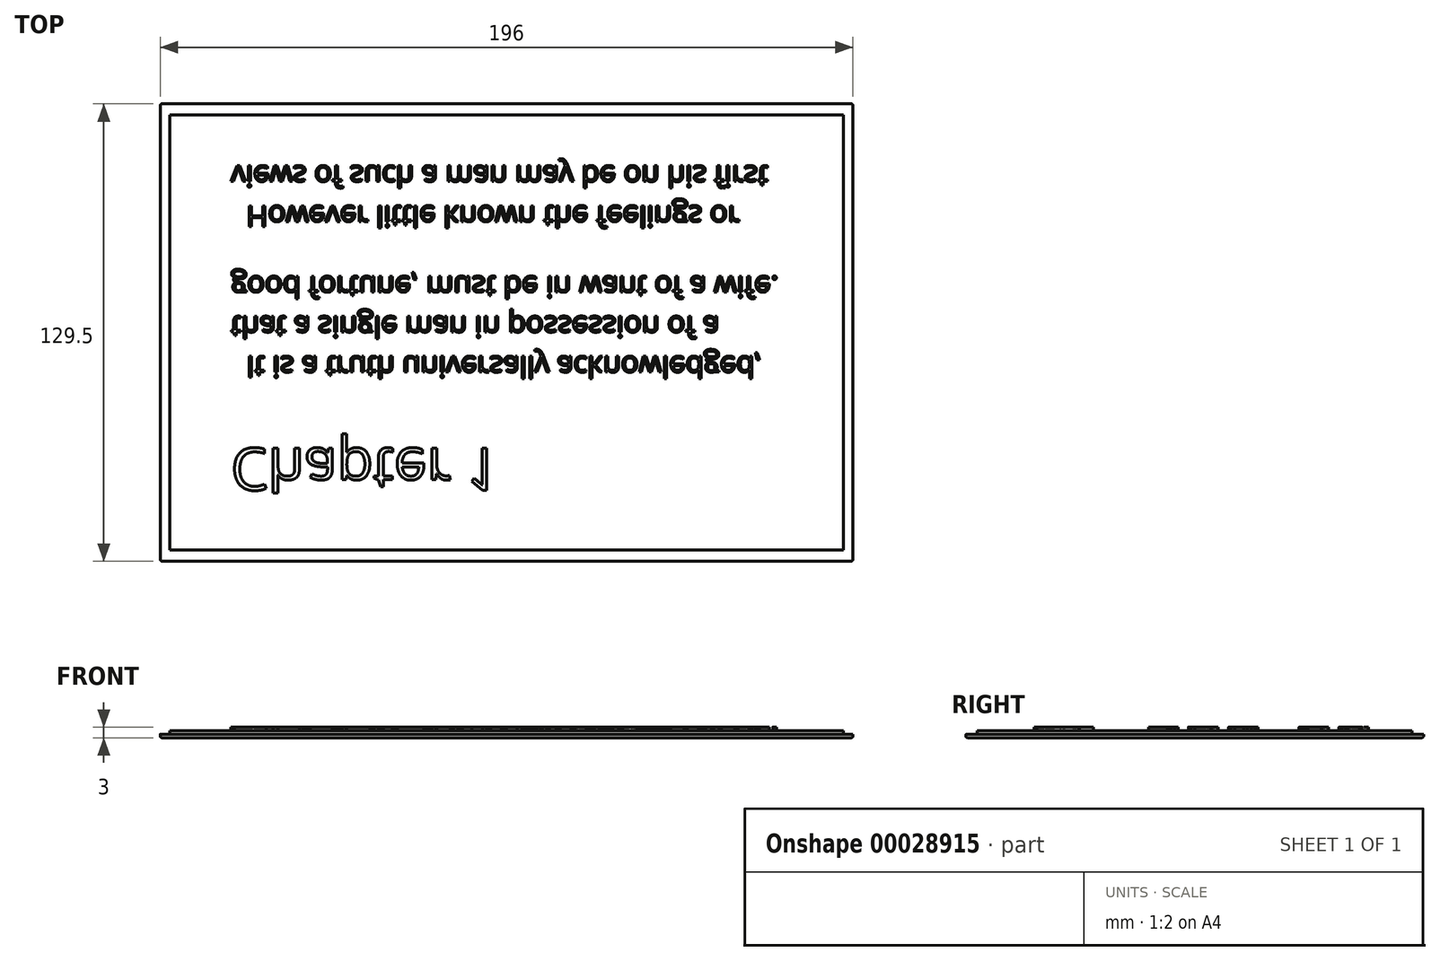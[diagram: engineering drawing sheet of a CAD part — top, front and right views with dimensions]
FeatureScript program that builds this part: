
annotation { "Feature Type Name" : "Feature", "Feature Type Description" : "" }
export const myFeature = defineFeature(function(context is Context, id is Id, definition is map)
    precondition{}
    {
        {
            assignVariable(context, id + "F0", {"name" : "TypeH", "anyValue" : 3});
        }
        {
            var Q0;
            Q0=qCreatedBy(makeId("Top.planeOp"),FACE);
            var sketch = newSketch(context, id + "F1", { "sketchPlane" : qUnion([Q0])});
            skLineSegment(sketch, "E0.bottom", {"start": v(0, 129.5) * mm, "end": v(196, 129.5) * mm});
            skLineSegment(sketch, "E0.top", {"start": v(0, 0) * mm, "end": v(196, 0) * mm});
            skLineSegment(sketch, "E0.left", {"start": v(0, 129.5) * mm, "end": v(0, 0) * mm});
            skLineSegment(sketch, "E0.right", {"start": v(196, 129.5) * mm, "end": v(196, 0) * mm});
            skSolve(sketch);
        }
        {
            var Q0;
            Q0=makeQuery(id+"F1.imprint","IMPRINT",FACE,{"disambiguationData":[TD([[makeQuery(id+"F1.imprint","IMPRINT",EDGE,{"derivedFrom":sQuery(id+"F1.wireOp",EDGE,"E0.bottom")}),-1.0]])]});
            extrude(context, id + "F2", {"entities" : qUnion([Q0]), "oppositeDirection" : true, "depth" : (getVariable(context, 'TypeH') - 1) * mm});
        }
        {
            var Q0;
            Q0=makeQuery(id+"F2.opExtrude","CAP_FACE",FACE,{"disambiguationData":[OSD([sQuery(id+"F1.wireOp",EDGE,"E0.bottom"),sQuery(id+"F1.wireOp",EDGE,"E0.top"),sQuery(id+"F1.wireOp",EDGE,"E0.left"),sQuery(id+"F1.wireOp",EDGE,"E0.right")])],"isStart":false});
            var sketch = newSketch(context, id + "F3", { "sketchPlane" : qUnion([Q0])});
            skLineSegment(sketch, "E1.bottom", {"start": v(2.7, -126.3) * mm, "end": v(193.3, -126.3) * mm});
            skLineSegment(sketch, "E1.top", {"start": v(2.7, -3.2) * mm, "end": v(193.3, -3.2) * mm});
            skLineSegment(sketch, "E1.left", {"start": v(2.7, -126.3) * mm, "end": v(2.7, -3.2) * mm});
            skLineSegment(sketch, "E1.right", {"start": v(193.3, -126.3) * mm, "end": v(193.3, -3.2) * mm});
            skSolve(sketch);
        }
        {
            var Q0;
            Q0=makeQuery(id+"F3.imprint","IMPRINT",FACE,{"disambiguationData":[TD([[makeQuery(id+"F3.imprint","IMPRINT",EDGE,{"derivedFrom":sQuery(id+"F3.wireOp",EDGE,"E1.bottom")}),-1.0]])]});
            extrude(context, id + "F4", {"entities" : qUnion([Q0]), "operationType" : NewBodyOperationType.REMOVE, "oppositeDirection" : true, "depth" : 1 * mm});
        }
        {
            var Q0;
            Q0=makeQuery(id+"F2.opExtrude","CAP_FACE",FACE,{"disambiguationData":[OSD([sQuery(id+"F1.wireOp",EDGE,"E0.bottom"),sQuery(id+"F1.wireOp",EDGE,"E0.top"),sQuery(id+"F1.wireOp",EDGE,"E0.left"),sQuery(id+"F1.wireOp",EDGE,"E0.right")])],"isStart":false});
            var sketch = newSketch(context, id + "F5", { "sketchPlane" : qUnion([Q0])});
            skText(sketch, "E2", { "text": "Chapter 1", "fontName": "OpenSans-Regular.ttf"});
            skLineSegment(sketch, "E3", {"start": v(20, -32) * mm, "end": v(20, -109.5) * mm, "construction": true});
            skText(sketch, "E4", { "text": "  It is a truth universally acknowledged,\nthat a single man in possession of a\ngood fortune, must be in want of a wife.", "fontName": "OpenSans-Regular.ttf"});
            skText(sketch, "E5", { "text": "  However little known the feelings or\nviews of such a man may be on his first", "fontName": "OpenSans-Regular.ttf"});
            const initialGuessF5  = {"E2": [0.02, -0.032, 1, 0, 0.012], "E4": [0.02, -0.058, 1, 0, 0.006], "E5": [0.02, -0.10063, 1, 0, 0.006]};
            skSetInitialGuess(sketch, initialGuessF5);
            skSolve(sketch);
        }
        {
            var Q0;
            Q0 = qSketchRegion(id + "F5", true);
            extrude(context, id + "F6", {"entities" : qUnion([Q0]), "operationType" : NewBodyOperationType.ADD, "depth" : 1 * mm});
        }
        {
            var Q0;
            Q0=makeQuery(id+"F2.opExtrude","SWEPT_BODY",BODY,{"disambiguationData":[OSD([sQuery(id+"F1.wireOp",EDGE,"E0.bottom"),sQuery(id+"F1.wireOp",EDGE,"E0.top"),sQuery(id+"F1.wireOp",EDGE,"E0.left"),sQuery(id+"F1.wireOp",EDGE,"E0.right")])]});
            var Q1;
            Q1=qCreatedBy(makeId("Top.planeOp"),FACE);
            mirror(context, id + "F7", {"entities" : qUnion([Q0]), "mirrorPlane" : qUnion([Q1])});
        }
        {
            var Q0;
            Q0=makeQuery(id+"F2.opExtrude","SWEPT_BODY",BODY,{"disambiguationData":[OSD([sQuery(id+"F1.wireOp",EDGE,"E0.bottom"),sQuery(id+"F1.wireOp",EDGE,"E0.top"),sQuery(id+"F1.wireOp",EDGE,"E0.left"),sQuery(id+"F1.wireOp",EDGE,"E0.right")])]});
            deleteBodies(context, id + "F8", {"entities" : qUnion([Q0])});
        }
        {
            var Q0;
            Q0=makeQuery(id+"F7.opPattern","COPY",EDGE,{"derivedFrom":makeQuery(id+"F2.opExtrude","SWEPT_EDGE",EDGE,{"disambiguationData":[OSD([sQuery(id+"F1.wireOp",EDGE,"E0.top"),sQuery(id+"F1.wireOp",EDGE,"E0.right")])]}),"instanceName":"1"});
            var Q1;
            Q1=makeQuery(id+"F7.opPattern","COPY",EDGE,{"derivedFrom":makeQuery(id+"F2.opExtrude","CAP_EDGE",EDGE,{"disambiguationData":[OSD([sQuery(id+"F1.wireOp",EDGE,"E0.top")])],"isStart":true}),"instanceName":"1"});
            var Q2;
            Q2=makeQuery(id+"F7.opPattern","COPY",EDGE,{"derivedFrom":makeQuery(id+"F2.opExtrude","CAP_EDGE",EDGE,{"disambiguationData":[OSD([sQuery(id+"F1.wireOp",EDGE,"E0.right")])],"isStart":true}),"instanceName":"1"});
            var Q3;
            Q3=makeQuery(id+"F7.opPattern","COPY",EDGE,{"derivedFrom":makeQuery(id+"F2.opExtrude","CAP_EDGE",EDGE,{"disambiguationData":[OSD([sQuery(id+"F1.wireOp",EDGE,"E0.bottom")])],"isStart":true}),"instanceName":"1"});
            var Q4;
            Q4=makeQuery(id+"F7.opPattern","COPY",EDGE,{"derivedFrom":makeQuery(id+"F2.opExtrude","CAP_EDGE",EDGE,{"disambiguationData":[OSD([sQuery(id+"F1.wireOp",EDGE,"E0.left")])],"isStart":true}),"instanceName":"1"});
            var Q5;
            Q5=makeQuery(id+"F7.opPattern","COPY",EDGE,{"derivedFrom":makeQuery(id+"F2.opExtrude","SWEPT_EDGE",EDGE,{"disambiguationData":[OSD([sQuery(id+"F1.wireOp",EDGE,"E0.top"),sQuery(id+"F1.wireOp",EDGE,"E0.left")])]}),"instanceName":"1"});
            var Q6;
            Q6=makeQuery(id+"F7.opPattern","COPY",EDGE,{"derivedFrom":makeQuery(id+"F2.opExtrude","SWEPT_EDGE",EDGE,{"disambiguationData":[OSD([sQuery(id+"F1.wireOp",EDGE,"E0.bottom"),sQuery(id+"F1.wireOp",EDGE,"E0.right")])]}),"instanceName":"1"});
            var Q7;
            Q7=makeQuery(id+"F7.opPattern","COPY",EDGE,{"derivedFrom":makeQuery(id+"F2.opExtrude","SWEPT_EDGE",EDGE,{"disambiguationData":[OSD([sQuery(id+"F1.wireOp",EDGE,"E0.bottom"),sQuery(id+"F1.wireOp",EDGE,"E0.left")])]}),"instanceName":"1"});
            var Q8;
            Q8=makeQuery(id+"F4.boolean.opBoolean","COPY",EDGE,{"derivedFrom":makeQuery(id+"F4.opExtrude","SWEPT_EDGE",EDGE,{"disambiguationData":[OSD([sQuery(id+"F3.wireOp",EDGE,"E1.bottom"),sQuery(id+"F3.wireOp",EDGE,"E1.left")])]})});
            var Q9;
            Q9=makeQuery(id+"F4.boolean.opBoolean","COPY",EDGE,{"derivedFrom":makeQuery(id+"F4.opExtrude","SWEPT_EDGE",EDGE,{"disambiguationData":[OSD([sQuery(id+"F3.wireOp",EDGE,"E1.bottom"),sQuery(id+"F3.wireOp",EDGE,"E1.right")])]})});
            var Q10;
            Q10=makeQuery(id+"F4.boolean.opBoolean","COPY",EDGE,{"derivedFrom":makeQuery(id+"F4.opExtrude","SWEPT_EDGE",EDGE,{"disambiguationData":[OSD([sQuery(id+"F3.wireOp",EDGE,"E1.top"),sQuery(id+"F3.wireOp",EDGE,"E1.right")])]})});
            var Q11;
            Q11=makeQuery(id+"F4.boolean.opBoolean","COPY",EDGE,{"derivedFrom":makeQuery(id+"F4.opExtrude","SWEPT_EDGE",EDGE,{"disambiguationData":[OSD([sQuery(id+"F3.wireOp",EDGE,"E1.top"),sQuery(id+"F3.wireOp",EDGE,"E1.left")])]})});
            fillet(context, id + "F9", {"entities" : qUnion([Q0, Q1, Q2, Q3, Q4, Q5, Q6, Q7, Q8, Q9, Q10, Q11]), "radius" : 0.5 * mm, "tangentPropagation" : true, "allowEdgeOverflow" : false});
        }
    });
